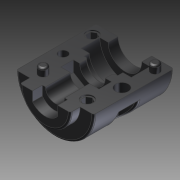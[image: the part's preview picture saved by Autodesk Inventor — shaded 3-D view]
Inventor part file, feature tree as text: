
AUTODESK INVENTOR PART (.ipt)
format: ipt  version: 2014 SP1 (Build 180222100, 222)  size: 249,856 bytes
history: native  units: in
note: dims shown in document units (in); Inventor stores cm internally (conversion verified against a paired STEP export)
features: fillet x1, other x1, imported_body x1
ambient origin geometry x8: Origin, YZ Plane, XZ Plane, XY Plane, X Axis, Y Axis, Z Axis, Center Point
bodies: Body1 (feature_tree)
feature tree (3):
  fillet  "Fillet1"  [1 undecoded]
  other  "217-3195-010 Rev1.ipt1"
  imported_body  "Base1"
note: 1 required parameter value undecoded (feature->parameter linkage not recoverable at this tier; creation-order binding heuristic only, values carry confidence <= 0.55)
